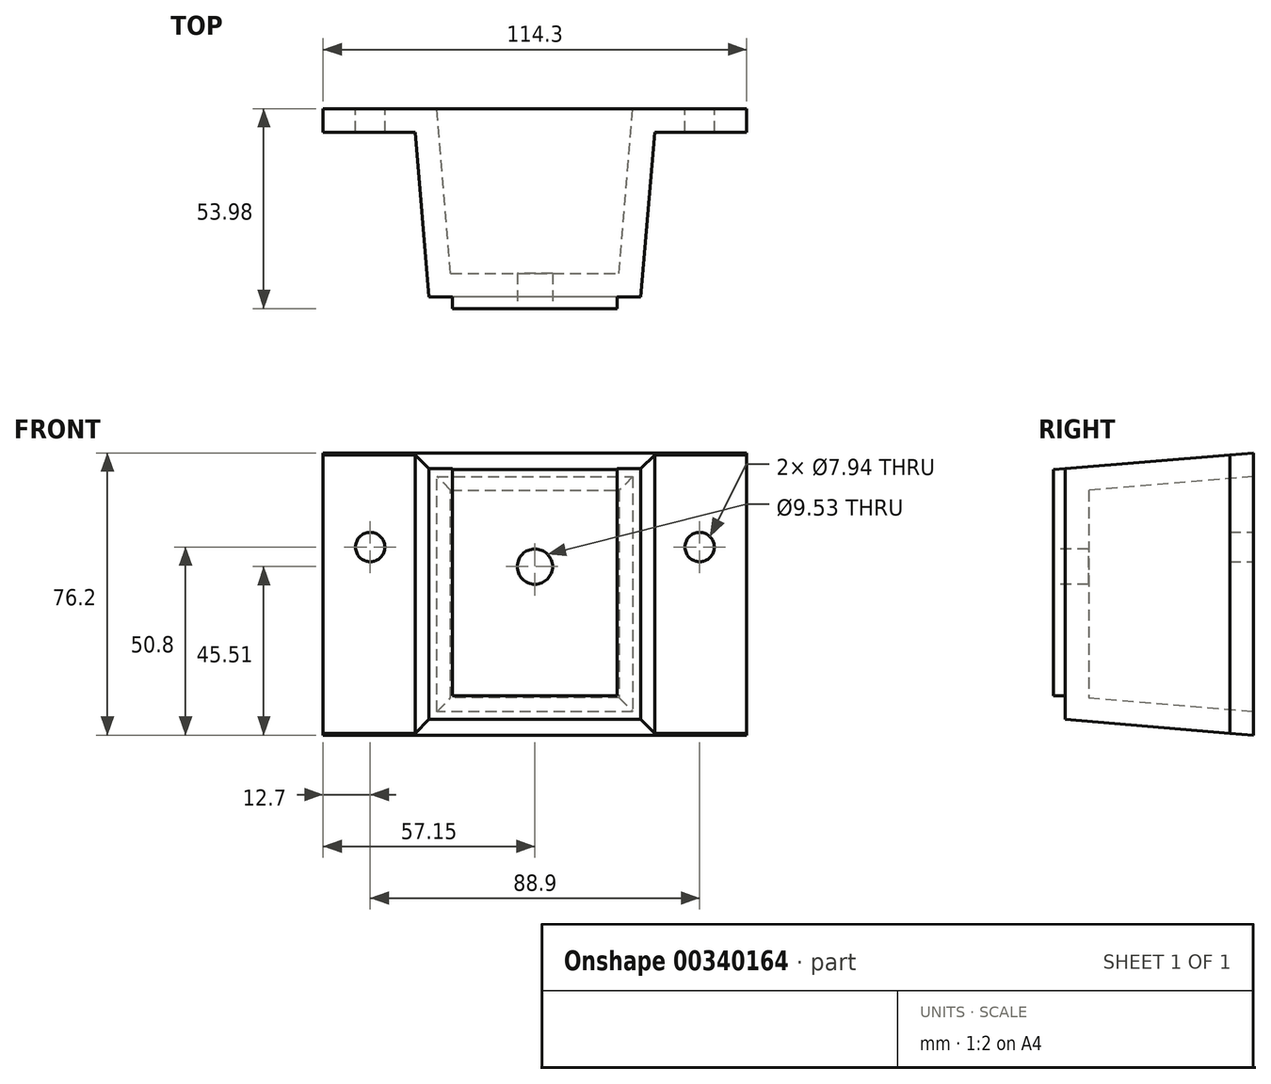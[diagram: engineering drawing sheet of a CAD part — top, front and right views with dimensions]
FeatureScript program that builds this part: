
annotation { "Feature Type Name" : "Feature", "Feature Type Description" : "" }
export const myFeature = defineFeature(function(context is Context, id is Id, definition is map)
    precondition{}
    {
        {
            var Q0;
            Q0=qCreatedBy(makeId("Front.planeOp"),FACE);
            var sketch = newSketch(context, id + "F0", { "sketchPlane" : qUnion([Q0])});
            skLineSegment(sketch, "E0.bottom", {"start": v(32.81, 38.1) * mm, "end": v(-32.81, 38.1) * mm});
            skLineSegment(sketch, "E0.top", {"start": v(32.81, -38.1) * mm, "end": v(-32.81, -38.1) * mm});
            skLineSegment(sketch, "E0.left", {"start": v(32.81, 38.1) * mm, "end": v(32.81, -38.1) * mm});
            skLineSegment(sketch, "E0.right", {"start": v(-32.81, 38.1) * mm, "end": v(-32.81, -38.1) * mm});
            skPoint(sketch, "E0.middle", {"position": v(0, 0) * mm});
            skLineSegment(sketch, "E1", {"start": v(-32.81, 38.1) * mm, "end": v(-32.81, 88.9) * mm, "construction": true});
            skLineSegment(sketch, "E2", {"start": v(-32.81, 88.9) * mm, "end": v(-35.99, 88.9) * mm, "construction": true});
            skLineSegment(sketch, "E3", {"start": v(-35.99, 88.9) * mm, "end": v(-32.81, 38.1) * mm, "construction": true});
            skSolve(sketch);
        }
        {
            var Q0;
            Q0 = qSketchRegion(id + "F0", true);
            extrude(context, id + "F1", {"entities" : qUnion([Q0]), "depth" : 50.8 * mm, "hasDraft" : true, "draftAngle" : 4.76 * degree, "draftPullDirection" : true});
        }
        {
            var Q0;
            Q0=makeQuery(id+"F1.opExtrude","CAP_FACE",FACE,{"disambiguationData":[OSD([sQuery(id+"F0.wireOp",EDGE,"E0.bottom"),sQuery(id+"F0.wireOp",EDGE,"E0.top"),sQuery(id+"F0.wireOp",EDGE,"E0.left"),sQuery(id+"F0.wireOp",EDGE,"E0.right")])],"isStart":true});
            shell(context, id + "F2", {"entities" : qUnion([Q0]), "thickness" : 6.35 * mm});
        }
        {
            var Q0;
            Q0=makeQuery(id+"F1.opExtrude","CAP_FACE",FACE,{"disambiguationData":[OSD([sQuery(id+"F0.wireOp",EDGE,"E0.bottom"),sQuery(id+"F0.wireOp",EDGE,"E0.top"),sQuery(id+"F0.wireOp",EDGE,"E0.left"),sQuery(id+"F0.wireOp",EDGE,"E0.right")])],"isStart":false});
            var sketch = newSketch(context, id + "F3", { "sketchPlane" : qUnion([Q0])});
            skLineSegment(sketch, "E4.0", {"start": v(22.23, 33.87) * mm, "end": v(22.23, -27.52) * mm});
            skLineSegment(sketch, "E4.1", {"start": v(22.23, -27.52) * mm, "end": v(-22.23, -27.52) * mm});
            skLineSegment(sketch, "E4.2", {"start": v(-22.23, 33.87) * mm, "end": v(-22.23, -27.52) * mm});
            skLineSegment(sketch, "E5.0.0", {"start": v(-28.58, -33.87) * mm, "end": v(28.58, -33.87) * mm});
            skLineSegment(sketch, "E5.0.1", {"start": v(28.58, -33.87) * mm, "end": v(28.58, 33.87) * mm});
            skLineSegment(sketch, "E5.0.2", {"start": v(28.58, 33.87) * mm, "end": v(-28.58, 33.87) * mm});
            skLineSegment(sketch, "E5.0.3", {"start": v(-28.58, 33.87) * mm, "end": v(-28.58, -33.87) * mm});
            skSolve(sketch);
        }
        {
            var Q0;
            {var subQ0=sQuery(id+"F3.wireOp",EDGE,"E4.0");Q0=makeQuery(id+"F3.imprint","IMPRINT",FACE,{"disambiguationData":[TD([[makeQuery(id+"F3.imprint","IMPRINT",EDGE,{"derivedFrom":subQ0}),-1.0]])]});}
            extrude(context, id + "F4", {"entities" : qUnion([Q0]), "operationType" : NewBodyOperationType.ADD, "depth" : 3.17 * mm});
        }
        {
            var Q0;
            Q0=qCreatedBy(makeId("Front.planeOp"),FACE);
            var sketch = newSketch(context, id + "F5", { "sketchPlane" : qUnion([Q0])});
            skLineSegment(sketch, "E6.0", {"start": v(26.44, -31.73) * mm, "end": v(-26.44, -31.73) * mm});
            skLineSegment(sketch, "E7.0", {"start": v(26.44, 31.73) * mm, "end": v(26.44, -31.73) * mm});
            skLineSegment(sketch, "E8.0", {"start": v(26.44, 31.73) * mm, "end": v(-26.44, 31.73) * mm});
            skLineSegment(sketch, "E9.0", {"start": v(-26.44, 31.73) * mm, "end": v(-26.44, -31.73) * mm});
            skLineSegment(sketch, "E10.0", {"start": v(32.81, -38.1) * mm, "end": v(-32.81, -38.1) * mm});
            skLineSegment(sketch, "E11.0", {"start": v(32.81, 38.1) * mm, "end": v(-32.81, 38.1) * mm});
            skLineSegment(sketch, "E12.bottom", {"start": v(57.15, -38.1) * mm, "end": v(-57.15, -38.1) * mm});
            skLineSegment(sketch, "E12.top", {"start": v(57.15, 38.1) * mm, "end": v(-57.15, 38.1) * mm});
            skLineSegment(sketch, "E12.left", {"start": v(57.15, -38.1) * mm, "end": v(57.15, 38.1) * mm});
            skLineSegment(sketch, "E12.right", {"start": v(-57.15, -38.1) * mm, "end": v(-57.15, 38.1) * mm});
            skPoint(sketch, "E12.middle", {"position": v(0, 0) * mm});
            skSolve(sketch);
        }
        {
            var Q0;
            Q0=makeQuery(id+"F5.imprint","IMPRINT",FACE,{"disambiguationData":[TD([[makeQuery(id+"F5.imprint","IMPRINT",EDGE,{"derivedFrom":sQuery(id+"F5.wireOp",EDGE,"E6.0")}),1.0]])]});
            extrude(context, id + "F6", {"entities" : qUnion([Q0]), "operationType" : NewBodyOperationType.ADD, "depth" : 6.35 * mm});
        }
        {
            var Q0;
            Q0=makeQuery(id+"F1.opExtrude","SWEPT_FACE",FACE,{"disambiguationData":[OSD([sQuery(id+"F0.wireOp",EDGE,"E0.bottom")])]});
            var sketch = newSketch(context, id + "F7", { "sketchPlane" : qUnion([Q0])});
            skCircle(sketch, "E13", {"center": v(28.58, -47.81) * mm, "radius": 127 * mm});
            skSolve(sketch);
        }
        {
            var Q0;
            Q0 = qSketchRegion(id + "F7", true);
            extrude(context, id + "F8", {"entities" : qUnion([Q0]), "operationType" : NewBodyOperationType.REMOVE, "endBound" : BoundingType.THROUGH_ALL, "depth" : 25.4 * mm});
        }
        {
            var Q0;
            Q0=makeQuery(id+"F1.opExtrude","SWEPT_FACE",FACE,{"disambiguationData":[OSD([sQuery(id+"F0.wireOp",EDGE,"E0.top")])]});
            var sketch = newSketch(context, id + "F9", { "sketchPlane" : qUnion([Q0])});
            skCircle(sketch, "E14", {"center": v(-28.58, 47.81) * mm, "radius": 114.3 * mm});
            skSolve(sketch);
        }
        {
            var Q0;
            Q0 = qSketchRegion(id + "F9", true);
            extrude(context, id + "F10", {"entities" : qUnion([Q0]), "operationType" : NewBodyOperationType.REMOVE, "endBound" : BoundingType.THROUGH_ALL, "depth" : 25.4 * mm});
        }
        {
            var Q0;
            Q0=makeQuery(id+"F6.boolean.opBoolean","MERGE",FACE,{"derivedFrom":[makeQuery(id+"F1.opExtrude","CAP_FACE",FACE,{"disambiguationData":[OSD([sQuery(id+"F0.wireOp",EDGE,"E0.bottom"),sQuery(id+"F0.wireOp",EDGE,"E0.top"),sQuery(id+"F0.wireOp",EDGE,"E0.left"),sQuery(id+"F0.wireOp",EDGE,"E0.right")])],"isStart":true}),makeQuery(id+"F6.opExtrude","CAP_FACE",FACE,{"disambiguationData":[OSD([sQuery(id+"F5.wireOp",EDGE,"E6.0"),sQuery(id+"F5.wireOp",EDGE,"E7.0"),sQuery(id+"F5.wireOp",EDGE,"E8.0"),sQuery(id+"F5.wireOp",EDGE,"E9.0"),sQuery(id+"F5.wireOp",EDGE,"E12.bottom"),sQuery(id+"F5.wireOp",EDGE,"E12.top"),sQuery(id+"F5.wireOp",EDGE,"E12.left"),sQuery(id+"F5.wireOp",EDGE,"E12.right")])],"isStart":true})]});
            var sketch = newSketch(context, id + "F11", { "sketchPlane" : qUnion([Q0])});
            skCircle(sketch, "E15", {"center": v(-44.45, 12.7) * mm, "radius": 3.97 * mm});
            skCircle(sketch, "E16", {"center": v(44.45, 12.7) * mm, "radius": 3.97 * mm});
            skSolve(sketch);
        }
        {
            var Q0;
            Q0 = qSketchRegion(id + "F11", true);
            extrude(context, id + "F12", {"entities" : qUnion([Q0]), "operationType" : NewBodyOperationType.REMOVE, "endBound" : BoundingType.THROUGH_ALL, "oppositeDirection" : true, "depth" : 25.4 * mm});
        }
        {
            var Q0;
            Q0=makeQuery(id+"F4.opExtrude","CAP_FACE",FACE,{"disambiguationData":[OSD([sQuery(id+"F3.wireOp",EDGE,"E4.0"),sQuery(id+"F3.wireOp",EDGE,"E4.1"),sQuery(id+"F3.wireOp",EDGE,"E4.2"),sQuery(id+"F3.wireOp",EDGE,"E5.0.2")])],"isStart":false});
            var sketch = newSketch(context, id + "F13", { "sketchPlane" : qUnion([Q0])});
            skCircle(sketch, "E17", {"center": v(0, 7.4) * mm, "radius": 4.76 * mm});
            skLineSegment(sketch, "E18.0", {"start": v(28.58, -33.87) * mm, "end": v(-28.58, -33.87) * mm});
            skLineSegment(sketch, "E19", {"start": v(0, -27.52) * mm, "end": v(0, 7.4) * mm, "construction": true});
            skSolve(sketch);
        }
        {
            var Q0;
            Q0 = qSketchRegion(id + "F13", true);
            extrude(context, id + "F14", {"entities" : qUnion([Q0]), "operationType" : NewBodyOperationType.REMOVE, "endBound" : BoundingType.THROUGH_ALL, "oppositeDirection" : true, "depth" : 25.4 * mm});
        }
    });
